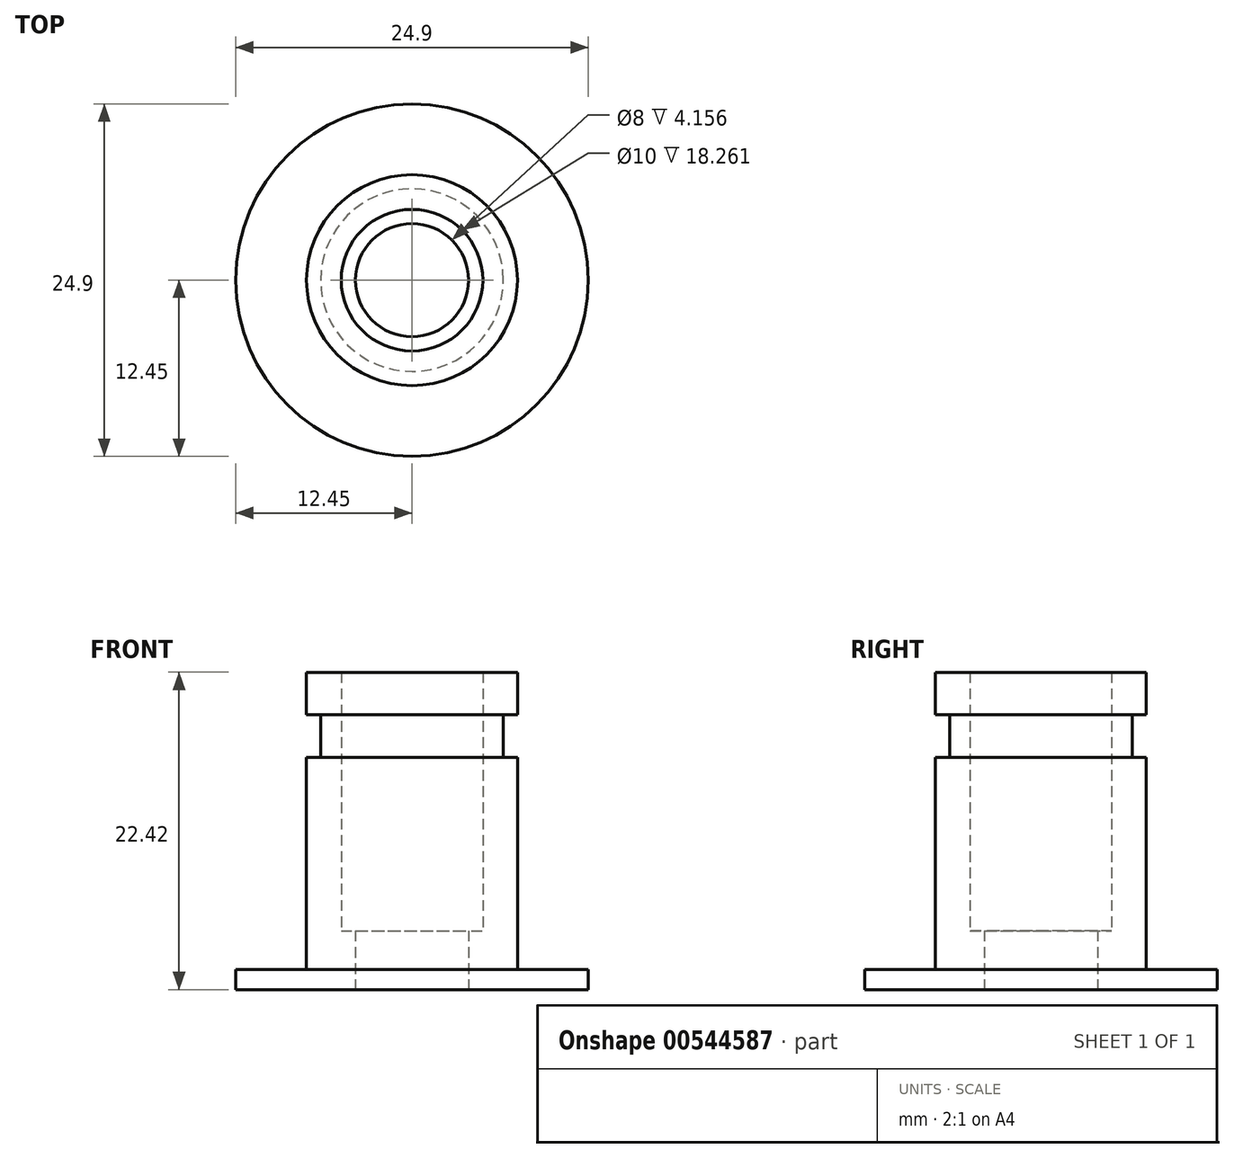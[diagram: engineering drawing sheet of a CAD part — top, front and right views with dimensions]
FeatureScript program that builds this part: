
annotation { "Feature Type Name" : "Feature", "Feature Type Description" : "" }
export const myFeature = defineFeature(function(context is Context, id is Id, definition is map)
    precondition{}
    {
        {
            var Q0;
            Q0=qCreatedBy(makeId("Front.planeOp"),FACE);
            var sketch = newSketch(context, id + "F0", { "sketchPlane" : qUnion([Q0])});
            skLineSegment(sketch, "E0", {"start": v(4, 0) * mm, "end": v(4, 4.16) * mm});
            skLineSegment(sketch, "E1", {"start": v(4, 4.16) * mm, "end": v(5, 4.16) * mm});
            skLineSegment(sketch, "E2", {"start": v(5, 4.16) * mm, "end": v(5, 22.42) * mm});
            skLineSegment(sketch, "E3", {"start": v(5, 22.42) * mm, "end": v(7.45, 22.42) * mm});
            skLineSegment(sketch, "E4", {"start": v(7.45, 22.42) * mm, "end": v(7.45, 19.42) * mm});
            skLineSegment(sketch, "E5", {"start": v(7.45, 19.42) * mm, "end": v(6.45, 19.42) * mm});
            skLineSegment(sketch, "E6", {"start": v(6.45, 19.42) * mm, "end": v(6.45, 16.42) * mm});
            skLineSegment(sketch, "E7", {"start": v(6.45, 16.42) * mm, "end": v(7.45, 16.42) * mm});
            skLineSegment(sketch, "E8", {"start": v(7.45, 16.42) * mm, "end": v(7.45, 1.42) * mm});
            skLineSegment(sketch, "E9", {"start": v(7.45, 1.42) * mm, "end": v(12.45, 1.42) * mm});
            skLineSegment(sketch, "E10", {"start": v(12.45, 1.42) * mm, "end": v(12.45, 0) * mm});
            skLineSegment(sketch, "E11", {"start": v(12.45, 0) * mm, "end": v(4, 0) * mm});
            skLineSegment(sketch, "E12", {"start": v(0, 0) * mm, "end": v(0, 16.74) * mm});
            skSolve(sketch);
        }
        {
            var Q0;
            Q0 = qSketchRegion(id + "F0", true);
            var Q1;
            Q1=sQuery(id+"F0.wireOp",EDGE,"E12");
            revolve(context, id + "F1", {"entities" : qUnion([Q0]), "axis" : qUnion([Q1]), "revolveType" : RevolveType.FULL});
        }
    });
